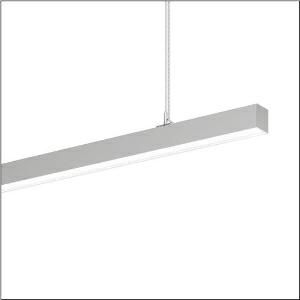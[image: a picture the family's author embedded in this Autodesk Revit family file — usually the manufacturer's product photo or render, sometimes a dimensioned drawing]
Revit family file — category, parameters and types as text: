
# Revit family: silica_r__21_51mx30dc49sb_4188
name_source: partatom
category: Lighting Fixtures
units: mm (PartAtom-declared; Revit-internal decimal feet)

## family parameters
Cut with Voids When Loaded = No
Host = Face
Light Source = No
Part Type = Normal
Room Calculation Point = No
Round Connector Dimension = Use Diameter
Shared = No

## types (1)
- --- (1 x LED, 10520 lm, 64.1 W, 4000K)
    Apparent Load = 64 VA
    CIE Flux Codes = 47 79 96 57 100
    Color Rendering = 80
    Color Temperature = 4000K
    Default Elevation = 1800 mm
    Description = Silica® 21, office luminaire, primary optical cover: cover, of PMMA, opal, light emission: direct/indirect distribution, primary light characteristic: symmetric, installation type: suspended mounting, LED, rated luminous flux: 10.520lm, luminous efficacy: 164lm/W, light colour: 840, colour temperature: 4000K, with terminal, 3+2-pole, max. 2.5mm², mains connection: 220..240V, AC, 50/60Hz, rated input power: 64.1W, luminaire housing, of aluminium, metallic grey (RAL 9006), length: 3.004mm, width: 53mm, height: 53mm, protection rating (complete): IP20, insulation class (complete): insulation class I (protective earthing), certification: CE, permissible operating ambient temperature: 0..+35°C, standard: EN 50419, packaging unit: 1 piece
    Height = 53 mm
    Lamp = 1 x LED
    Lamp Light Flux = 10520 lm
    Lamp Power = 64.1 W
    Lamp count = 1
    Length = 3004 mm
    Luminous efficacy = 164 lm/W
    Manufacturer = Siteco
    ModVariant = No
    Model = 51MX30DC49SB
    Mounting Place = Ceiling
    Mounting Type = Pendant
    Number of Poles = 1
    OnlyDefault = Yes
    Power Factor = 1
    Product Name = Silica® 21
    Product group = office luminaire | ceiling pendant
    ProductGroupID = 902
    Protection Class = Protection class I
    Protection Degree = IP 20
    RLX_Detail_Level = 1
    RLX_Emergency_Light_Flux = 0 lm
    RLX_Emergency_Type = 0
    RLX_Emergency_Type_DB = No
    RlxData = <blob elided: 23353 chars, md5=33c3b044>
    Socket = socket
    Standby Power = 0 W
    System Light Flux = 10520 lm
    System Power = 64 W
    Type Comments = factory setting: luminous flux: 100 % | dim-lin: 254 | 218 mA
    Type Image = l_1313621.jpg
    URL = http://relux.com
    VarID = @adj_065301
    Voltage = 0 V
    Weight = 0.00 kg
    Width = 53 mm

## geometry (parser evidence)
native form markers: Blend x4, Sweep x12
no freeform markers — native parametric forms only
